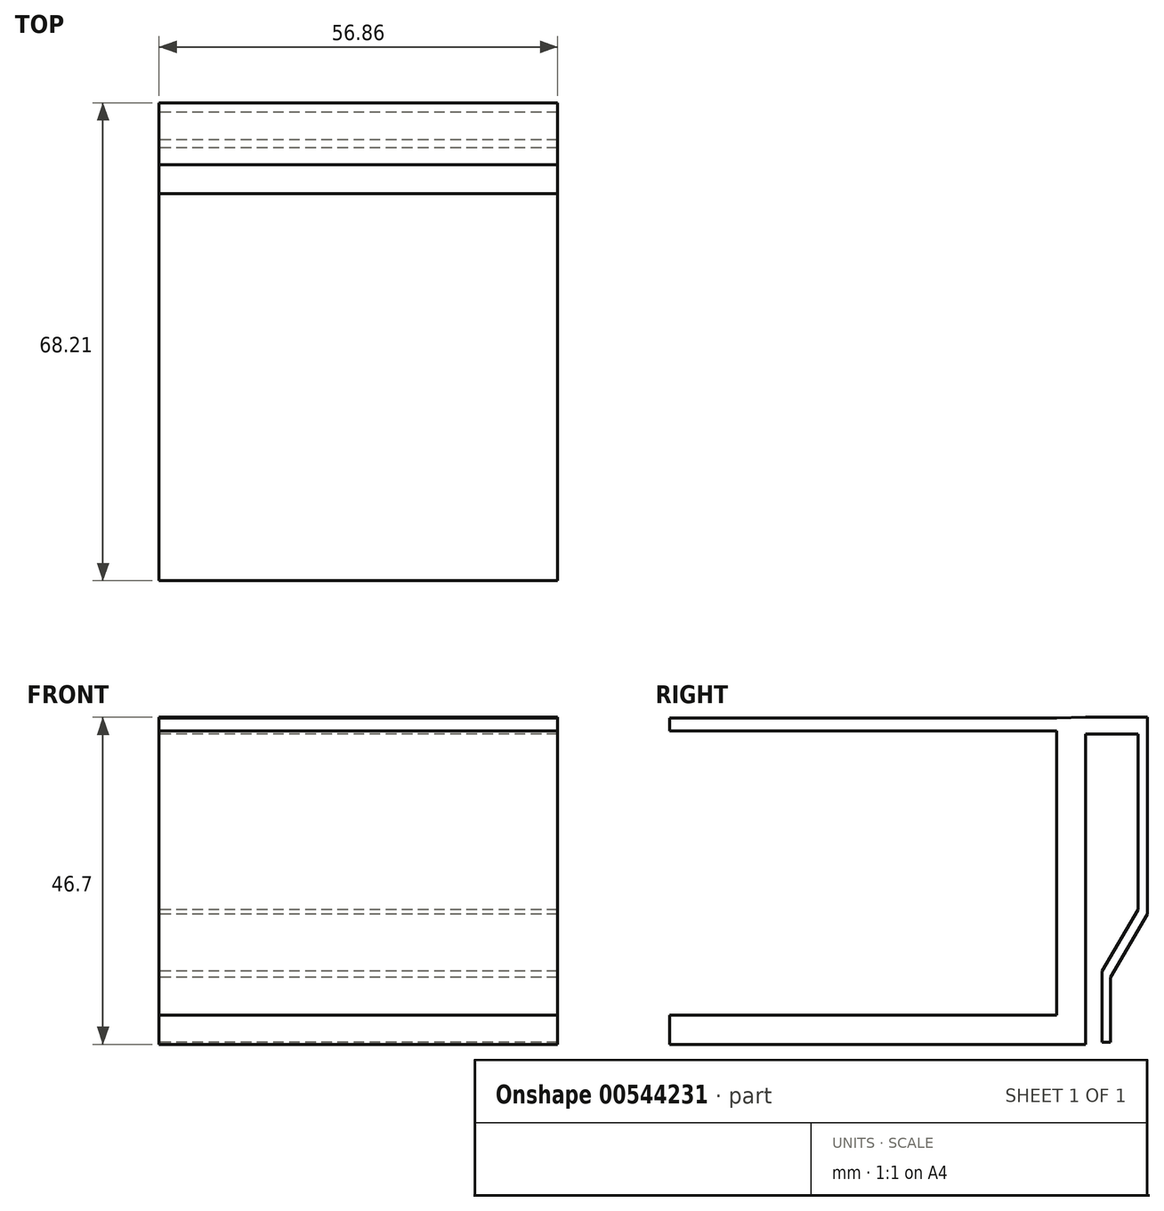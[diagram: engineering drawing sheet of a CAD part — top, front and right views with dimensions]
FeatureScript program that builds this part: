
annotation { "Feature Type Name" : "Feature", "Feature Type Description" : "" }
export const myFeature = defineFeature(function(context is Context, id is Id, definition is map)
    precondition{}
    {
        {
            var Q0;
            Q0=qCreatedBy(makeId("Right.planeOp"),FACE);
            var sketch = newSketch(context, id + "F0", { "sketchPlane" : qUnion([Q0])});
            skLineSegment(sketch, "E0", {"start": v(0, 17.96) * mm, "end": v(8.85, 17.96) * mm});
            skLineSegment(sketch, "E1", {"start": v(8.85, 17.96) * mm, "end": v(8.85, -10.13) * mm});
            skLineSegment(sketch, "E2", {"start": v(8.85, -10.13) * mm, "end": v(3.57, -19.19) * mm});
            skLineSegment(sketch, "E3", {"start": v(3.57, -19.19) * mm, "end": v(3.57, -28.44) * mm});
            skLineSegment(sketch, "E4", {"start": v(3.57, -28.44) * mm, "end": v(2.4, -28.44) * mm});
            skLineSegment(sketch, "E5", {"start": v(2.4, -28.44) * mm, "end": v(2.4, -18.28) * mm});
            skLineSegment(sketch, "E6", {"start": v(2.4, -18.28) * mm, "end": v(7.5, -9.54) * mm});
            skLineSegment(sketch, "E7", {"start": v(7.5, -9.54) * mm, "end": v(7.5, 15.54) * mm});
            skLineSegment(sketch, "E8", {"start": v(7.5, 15.54) * mm, "end": v(0, 15.54) * mm});
            skLineSegment(sketch, "E9", {"start": v(0, 15.54) * mm, "end": v(0, -28.74) * mm});
            skLineSegment(sketch, "E10", {"start": v(0, -28.74) * mm, "end": v(-4.1, -28.74) * mm});
            skLineSegment(sketch, "E11", {"start": v(-4.1, -28.74) * mm, "end": v(-4.1, 17.85) * mm});
            skLineSegment(sketch, "E12", {"start": v(-4.1, 17.85) * mm, "end": v(0, 17.96) * mm});
            skSolve(sketch);
        }
        {
            var Q0;
            Q0=makeQuery(id+"F0.imprint","IMPRINT",FACE,{"disambiguationData":[TD([[makeQuery(id+"F0.imprint","IMPRINT",EDGE,{"derivedFrom":sQuery(id+"F0.wireOp",EDGE,"E0")}),-1.0]])]});
            extrude(context, id + "F1", {"entities" : qUnion([Q0]), "depth" : 56.86 * mm, "offsetDistance" : 25 * mm});
        }
        {
            var Q0;
            Q0=makeQuery(id+"F1.opExtrude","SWEPT_FACE",FACE,{"disambiguationData":[OSD([sQuery(id+"F0.wireOp",EDGE,"E11")])]});
            var sketch = newSketch(context, id + "F2", { "sketchPlane" : qUnion([Q0])});
            skLineSegment(sketch, "E13.bottom", {"start": v(0, 17.85) * mm, "end": v(56.86, 17.85) * mm});
            skLineSegment(sketch, "E13.top", {"start": v(0, 16.03) * mm, "end": v(56.86, 16.03) * mm});
            skLineSegment(sketch, "E13.left", {"start": v(0, 17.85) * mm, "end": v(0, 16.03) * mm});
            skLineSegment(sketch, "E13.right", {"start": v(56.86, 17.85) * mm, "end": v(56.86, 16.03) * mm});
            skLineSegment(sketch, "E14.bottom", {"start": v(0, -28.74) * mm, "end": v(56.86, -28.74) * mm});
            skLineSegment(sketch, "E14.top", {"start": v(0, -24.6) * mm, "end": v(56.86, -24.6) * mm});
            skLineSegment(sketch, "E14.left", {"start": v(0, -28.74) * mm, "end": v(0, -24.6) * mm});
            skLineSegment(sketch, "E14.right", {"start": v(56.86, -28.74) * mm, "end": v(56.86, -24.6) * mm});
            skSolve(sketch);
        }
        {
            var Q0;
            Q0 = qSketchRegion(id + "F2", true);
            extrude(context, id + "F3", {"entities" : qUnion([Q0]), "operationType" : NewBodyOperationType.ADD, "depth" : 55.26 * mm, "offsetDistance" : 25 * mm});
        }
    });
